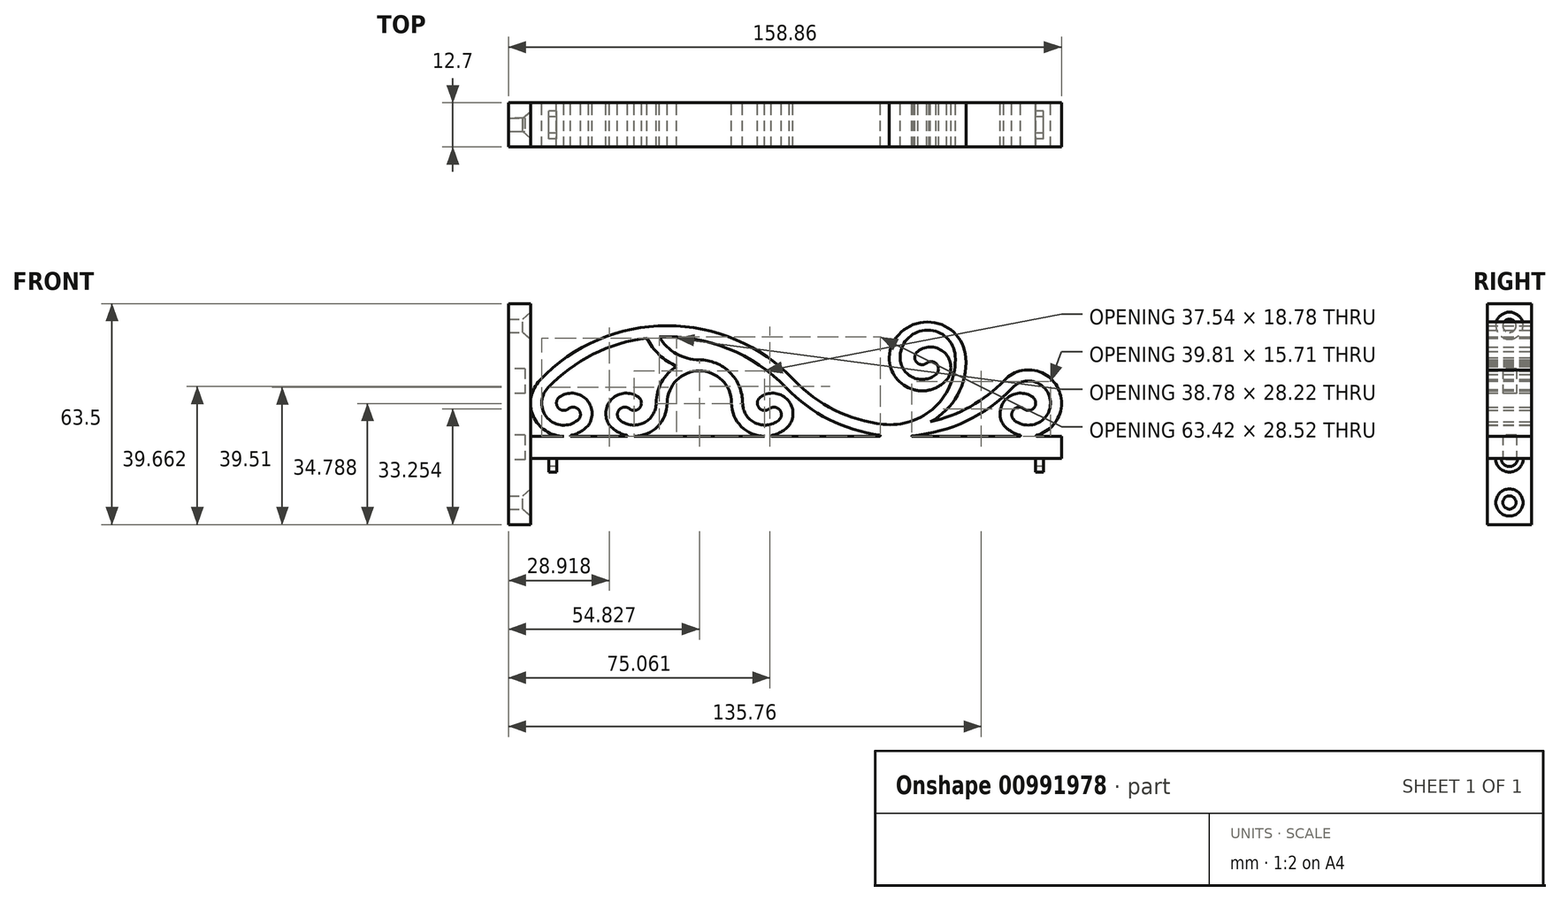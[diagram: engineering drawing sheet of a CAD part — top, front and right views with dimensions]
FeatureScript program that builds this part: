
annotation { "Feature Type Name" : "Feature", "Feature Type Description" : "" }
export const myFeature = defineFeature(function(context is Context, id is Id, definition is map)
    precondition{}
    {
        {
            var Q0;
            Q0=qCreatedBy(makeId("Front.planeOp"),FACE);
            var sketch = newSketch(context, id + "F0", { "sketchPlane" : qUnion([Q0])});
            skLineSegment(sketch, "E0.bottom", {"start": v(-3.17, 31.75) * mm, "end": v(3.18, 31.75) * mm, "construction": true});
            skLineSegment(sketch, "E0.top", {"start": v(-3.17, -31.75) * mm, "end": v(3.18, -31.75) * mm, "construction": true});
            skLineSegment(sketch, "E0.right", {"start": v(3.18, 31.75) * mm, "end": v(3.18, -31.75) * mm});
            skPoint(sketch, "E0.middle", {"position": v(0, 0) * mm});
            skLineSegment(sketch, "E1", {"start": v(3.18, 31.75) * mm, "end": v(-3.17, 31.75) * mm});
            skLineSegment(sketch, "E2", {"start": v(3.18, -31.75) * mm, "end": v(-3.17, -31.75) * mm});
            skLineSegment(sketch, "E3", {"start": v(-3.17, 31.75) * mm, "end": v(-3.17, -31.75) * mm});
            skSolve(sketch);
        }
        {
            var Q0;
            Q0=makeQuery(id+"F0.imprint","IMPRINT",FACE,{"disambiguationData":[TD([[makeQuery(id+"F0.imprint","IMPRINT",EDGE,{"derivedFrom":sQuery(id+"F0.wireOp",EDGE,"E0.right")}),-1.0]])]});
            extrude(context, id + "F1", {"entities" : qUnion([Q0]), "endBound" : BoundingType.SYMMETRIC, "depth" : 12.7 * mm});
        }
        {
            var Q0;
            Q0=makeQuery(id+"F1.opExtrude","SWEPT_FACE",FACE,{"disambiguationData":[OSD([sQuery(id+"F0.wireOp",EDGE,"E3")])]});
            var sketch = newSketch(context, id + "F2", { "sketchPlane" : qUnion([Q0])});
            skLineSegment(sketch, "E4", {"start": v(0, 9.53) * mm, "end": v(0, -9.53) * mm, "construction": true});
            skLineSegment(sketch, "E5.bottom", {"start": v(-1.97, 13.08) * mm, "end": v(1.97, 13.08) * mm});
            skLineSegment(sketch, "E5.top", {"start": v(-1.97, 5.97) * mm, "end": v(1.97, 5.97) * mm});
            skLineSegment(sketch, "E5.left", {"start": v(-1.97, 13.08) * mm, "end": v(-1.97, 5.97) * mm});
            skLineSegment(sketch, "E5.right", {"start": v(1.97, 13.08) * mm, "end": v(1.97, 5.97) * mm});
            skPoint(sketch, "E5.middle", {"position": v(0, 9.53) * mm});
            skLineSegment(sketch, "E6.bottom", {"start": v(-1.97, -5.97) * mm, "end": v(1.97, -5.97) * mm});
            skLineSegment(sketch, "E6.top", {"start": v(-1.97, -13.08) * mm, "end": v(1.97, -13.08) * mm});
            skLineSegment(sketch, "E6.left", {"start": v(-1.97, -5.97) * mm, "end": v(-1.97, -13.08) * mm});
            skLineSegment(sketch, "E6.right", {"start": v(1.97, -5.97) * mm, "end": v(1.97, -13.08) * mm});
            skPoint(sketch, "E6.middle", {"position": v(0, -9.53) * mm});
            skSolve(sketch);
        }
        {
            var Q0;
            Q0=makeQuery(id+"F2.imprint","IMPRINT",FACE,{"disambiguationData":[TD([[makeQuery(id+"F2.imprint","IMPRINT",EDGE,{"derivedFrom":sQuery(id+"F2.wireOp",EDGE,"E5.bottom")}),-1.0]])]});
            var Q1;
            Q1=makeQuery(id+"F2.imprint","IMPRINT",FACE,{"disambiguationData":[TD([[makeQuery(id+"F2.imprint","IMPRINT",EDGE,{"derivedFrom":sQuery(id+"F2.wireOp",EDGE,"E6.bottom")}),-1.0]])]});
            extrude(context, id + "F3", {"entities" : qUnion([Q0, Q1]), "operationType" : NewBodyOperationType.REMOVE, "oppositeDirection" : true, "depth" : 4.76 * mm});
        }
        {
            var Q0;
            Q0=makeQuery(id+"F1.opExtrude","SWEPT_FACE",FACE,{"disambiguationData":[OSD([sQuery(id+"F0.wireOp",EDGE,"E0.right")])]});
            var sketch = newSketch(context, id + "F4", { "sketchPlane" : qUnion([Q0])});
            skLineSegment(sketch, "E7", {"start": v(0, 25.4) * mm, "end": v(0, -25.4) * mm, "construction": true});
            skPoint(sketch, "E8", {"position": v(0, 25.4) * mm});
            skPoint(sketch, "E9", {"position": v(0, -25.4) * mm});
            skSolve(sketch);
        }
        {
            var Q0;
            Q0=sQuery(id+"F4.wireOp",VERTEX,"E8");
            var Q1;
            Q1=sQuery(id+"F4.wireOp",VERTEX,"E9");
            var Q2;
            Q2=makeQuery(id+"F1.opExtrude","SWEPT_BODY",BODY,{"disambiguationData":[OSD([sQuery(id+"F0.wireOp",EDGE,"E0.right"),sQuery(id+"F0.wireOp",EDGE,"E1"),sQuery(id+"F0.wireOp",EDGE,"E2"),sQuery(id+"F0.wireOp",EDGE,"E3")])]});
            hole(context, id + "F5", {"style" : HoleStyle.C_SINK, "endStyle" : HoleEndStyle.THROUGH, "standardTappedOrClearance" : lookupTablePath({ "standard" : "ANSI", "fit" : "Normal (ASME)", "size" : "#6", "type" : "Clearance" }), "standardBlindInLast" : lookupTablePath({ "fit" : "Free", "standard" : "ANSI", "size" : "#6", "type" : "Clearance" }), "holeDiameter" : 3.8 * mm, "cSinkDiameter" : 7.8 * mm, "cSinkAngle" : 82 * degree, "isTappedThrough" : true, "tappedDepth" : 12.7 * mm, "tapClearance" : 3, "locations" : qUnion([Q0, Q1]), "scope" : qUnion([Q2])});
        }
        {
            var Q0;
            Q0=makeQuery(id+"F1.opExtrude","SWEPT_FACE",FACE,{"disambiguationData":[OSD([sQuery(id+"F0.wireOp",EDGE,"E0.right")])]});
            var sketch = newSketch(context, id + "F6", { "sketchPlane" : qUnion([Q0])});
            skLineSegment(sketch, "E10.bottom", {"start": v(-6.35, 12.7) * mm, "end": v(6.35, 12.7) * mm});
            skLineSegment(sketch, "E10.top", {"start": v(-6.35, -12.7) * mm, "end": v(6.35, -12.7) * mm});
            skLineSegment(sketch, "E10.left", {"start": v(-6.35, 12.7) * mm, "end": v(-6.35, -12.7) * mm});
            skLineSegment(sketch, "E10.right", {"start": v(6.35, 12.7) * mm, "end": v(6.35, -12.7) * mm});
            skPoint(sketch, "E10.middle", {"position": v(0, 0) * mm});
            skSolve(sketch);
        }
        {
            var Q0;
            Q0=qCreatedBy(makeId("Front.planeOp"),FACE);
            var sketch = newSketch(context, id + "F7", { "sketchPlane" : qUnion([Q0])});
            skLineSegment(sketch, "E11.bottom", {"start": v(3.18, -6.35) * mm, "end": v(12.7, -6.35) * mm});
            skLineSegment(sketch, "E11.top", {"start": v(3.18, -12.7) * mm, "end": v(14.29, -12.7) * mm});
            skLineSegment(sketch, "E11.left", {"start": v(3.18, -6.35) * mm, "end": v(3.18, -12.7) * mm});
            skLineSegment(sketch, "E11.right", {"start": v(155.68, -6.35) * mm, "end": v(155.68, -12.7) * mm});
            skLineSegment(sketch, "E12", {"start": v(0, 0) * mm, "end": v(3.22, 0) * mm, "construction": true});
            skArc(sketch, "E13", {"start": v(5.8, 9.75) * mm, "mid": v(3.94, -0.57) * mm, "end": v(12.7, -6.35) * mm});
            skArc(sketch, "E14", {"start": v(8.1, 7.56) * mm, "mid": v(8.03, -1.13) * mm, "end": v(16.69, -1.77) * mm});
            skArc(sketch, "E15", {"start": v(11.44, 4.87) * mm, "mid": v(11.03, 1.88) * mm, "end": v(14.03, 1.53) * mm});
            skArc(sketch, "E16", {"start": v(16.69, -1.77) * mm, "mid": v(17, 1.21) * mm, "end": v(14.03, 1.53) * mm});
            skArc(sketch, "E17", {"start": v(19.77, -3.21) * mm, "mid": v(19.04, 4.36) * mm, "end": v(11.44, 4.87) * mm});
            skArc(sketch, "E18", {"start": v(78.9, 9.75) * mm, "mid": v(42.36, 25.4) * mm, "end": v(5.8, 9.75) * mm});
            skArc(sketch, "E19", {"start": v(76.6, 7.56) * mm, "mid": v(59.98, 18.82) * mm, "end": v(40.17, 22.17) * mm});
            skLineSegment(sketch, "E20", {"start": v(42.36, 25.4) * mm, "end": v(79.43, 25.4) * mm, "construction": true});
            skLineSegment(sketch, "E21", {"start": v(79.43, -6.35) * mm, "end": v(79.43, 38.2) * mm, "construction": true});
            skArc(sketch, "E22.MirrorCS", {"start": v(141.55, 7.56) * mm, "mid": v(152.49, 3.59) * mm, "end": v(142.16, -1.77) * mm});
            skArc(sketch, "E23.MirrorC", {"start": v(139.26, 9.75) * mm, "mid": v(154.38, 7.97) * mm, "end": v(148.47, -6.06) * mm});
            skArc(sketch, "E24.MirrorCS", {"start": v(147.4, 4.87) * mm, "mid": v(147.82, 1.88) * mm, "end": v(144.82, 1.53) * mm});
            skArc(sketch, "E25.MirrorCS", {"start": v(142.16, -1.77) * mm, "mid": v(141.84, 1.21) * mm, "end": v(144.82, 1.53) * mm});
            skArc(sketch, "E26.MirrorCS", {"start": v(139.08, -3.21) * mm, "mid": v(139.81, 4.36) * mm, "end": v(147.4, 4.87) * mm});
            skArc(sketch, "E27", {"start": v(78.9, 9.75) * mm, "mid": v(90.56, 1.17) * mm, "end": v(104.44, -2.92) * mm});
            skArc(sketch, "E28", {"start": v(76.6, 7.56) * mm, "mid": v(88.85, -1.53) * mm, "end": v(103.44, -6) * mm});
            skPoint(sketch, "E29.orphan", {"position": v(18.91, 4.48) * mm});
            skPoint(sketch, "E30.orphan", {"position": v(139.94, 4.48) * mm});
            skArc(sketch, "E31", {"start": v(103.41, -6.35) * mm, "mid": v(103.6, -6.18) * mm, "end": v(103.44, -6) * mm});
            skArc(sketch, "E32", {"start": v(112.74, -6.2) * mm, "mid": v(112.67, -6.28) * mm, "end": v(112.75, -6.35) * mm});
            skArc(sketch, "E33.trimOffspring", {"start": v(112.74, -6.2) * mm, "mid": v(128.41, -1.97) * mm, "end": v(141.55, 7.56) * mm});
            skLineSegment(sketch, "E34.trimOffspring", {"start": v(112.75, -6.35) * mm, "end": v(143.75, -6.35) * mm});
            skArc(sketch, "E35", {"start": v(148.47, -6.06) * mm, "mid": v(148.36, -6.22) * mm, "end": v(148.5, -6.35) * mm});
            skArc(sketch, "E36", {"start": v(143.75, -6.35) * mm, "mid": v(143.9, -6.22) * mm, "end": v(143.8, -6.05) * mm});
            skArc(sketch, "E37.trimOffspring", {"start": v(143.8, -6.05) * mm, "mid": v(141.23, -4.98) * mm, "end": v(139.08, -3.21) * mm});
            skLineSegment(sketch, "E38.trimOffspring", {"start": v(148.5, -6.35) * mm, "end": v(155.68, -6.35) * mm});
            skLineSegment(sketch, "E39", {"start": v(12.7, -6.35) * mm, "end": v(12.7, -6.35) * mm});
            skArc(sketch, "E40", {"start": v(14.67, -6.14) * mm, "mid": v(14.58, -6.26) * mm, "end": v(14.69, -6.35) * mm});
            skArc(sketch, "E41.trimOffspring", {"start": v(14.67, -6.14) * mm, "mid": v(17.45, -5.08) * mm, "end": v(19.77, -3.21) * mm});
            skLineSegment(sketch, "E42.trimOffspring", {"start": v(14.69, -6.35) * mm, "end": v(70.42, -6.35) * mm});
            skLineSegment(sketch, "E43", {"start": v(42.36, 25.4) * mm, "end": v(3.22, 25.4) * mm, "construction": true});
            skLineSegment(sketch, "E44", {"start": v(22.79, 25.4) * mm, "end": v(22.79, -6.35) * mm, "construction": true});
            skArc(sketch, "E45.MirrorCS", {"start": v(28.9, -1.77) * mm, "mid": v(28.57, 1.21) * mm, "end": v(31.55, 1.53) * mm});
            skLineSegment(sketch, "E46.MirrorCS", {"start": v(32.88, -6.35) * mm, "end": v(32.88, -6.35) * mm});
            skPoint(sketch, "E47.MirrorP", {"position": v(26.66, 4.48) * mm});
            skArc(sketch, "E48.MirrorCS", {"start": v(30.91, -6.14) * mm, "mid": v(31, -6.26) * mm, "end": v(30.9, -6.35) * mm});
            skLineSegment(sketch, "E49.MirrorCS", {"start": v(42.4, -6.35) * mm, "end": v(32.88, -6.35) * mm});
            skLineSegment(sketch, "E50.MirrorCS", {"start": v(45.58, 0) * mm, "end": v(42.36, 0) * mm, "construction": true});
            skArc(sketch, "E51.MirrorCS", {"start": v(39.23, 3.18) * mm, "mid": v(35.62, -2.55) * mm, "end": v(28.9, -1.77) * mm});
            skArc(sketch, "E52.MirrorCS", {"start": v(30.91, -6.14) * mm, "mid": v(28.13, -5.08) * mm, "end": v(25.81, -3.21) * mm});
            skArc(sketch, "E53.MirrorCS", {"start": v(34.13, 4.87) * mm, "mid": v(34.55, 1.88) * mm, "end": v(31.55, 1.53) * mm});
            skArc(sketch, "E54.MirrorCS", {"start": v(25.81, -3.21) * mm, "mid": v(26.54, 4.36) * mm, "end": v(34.13, 4.87) * mm});
            skLineSegment(sketch, "E55", {"start": v(42.36, 25.4) * mm, "end": v(42.4, -6.35) * mm, "construction": true});
            skLineSegment(sketch, "E56", {"start": v(60.9, 25.4) * mm, "end": v(60.9, -6.35) * mm, "construction": true});
            skLineSegment(sketch, "E57", {"start": v(60.9, 25.4) * mm, "end": v(42.4, -6.35) * mm, "construction": true});
            skLineSegment(sketch, "E58", {"start": v(51.65, 9.53) * mm, "end": v(51.65, 17.18) * mm, "construction": true});
            skArc(sketch, "E59.MirrorCS", {"start": v(64.07, 3.18) * mm, "mid": v(67.68, -2.55) * mm, "end": v(74.4, -1.77) * mm});
            skArc(sketch, "E60.MirrorCS", {"start": v(74.4, -1.77) * mm, "mid": v(74.72, 1.21) * mm, "end": v(71.74, 1.53) * mm});
            skArc(sketch, "E61.MirrorCS", {"start": v(72.38, -6.14) * mm, "mid": v(75.16, -5.08) * mm, "end": v(77.48, -3.21) * mm});
            skLineSegment(sketch, "E62.MirrorCS", {"start": v(70.42, -6.35) * mm, "end": v(70.42, -6.35) * mm});
            skPoint(sketch, "E63.MirrorP", {"position": v(76.63, 4.48) * mm});
            skArc(sketch, "E64.MirrorCS", {"start": v(69.16, 4.87) * mm, "mid": v(68.74, 1.88) * mm, "end": v(71.74, 1.53) * mm});
            skArc(sketch, "E65.MirrorCS", {"start": v(72.38, -6.14) * mm, "mid": v(72.3, -6.26) * mm, "end": v(72.4, -6.35) * mm});
            skArc(sketch, "E66.MirrorCS", {"start": v(77.48, -3.21) * mm, "mid": v(76.75, 4.36) * mm, "end": v(69.16, 4.87) * mm});
            skLineSegment(sketch, "E67.MirrorCS", {"start": v(60.9, -6.35) * mm, "end": v(70.42, -6.35) * mm});
            skArc(sketch, "E68", {"start": v(60.9, 3.18) * mm, "mid": v(51.64, 12.43) * mm, "end": v(42.39, 3.18) * mm});
            skArc(sketch, "E69", {"start": v(64.07, 3.18) * mm, "mid": v(60.42, 11.97) * mm, "end": v(51.62, 15.6) * mm});
            skLineSegment(sketch, "E70", {"start": v(51.65, 9.53) * mm, "end": v(26.5, 9.75) * mm, "construction": true});
            skArc(sketch, "E71", {"start": v(40.17, 22.17) * mm, "mid": v(45.01, 17.35) * mm, "end": v(51.62, 15.6) * mm});
            skArc(sketch, "E72", {"start": v(36.56, 21.87) * mm, "mid": v(40.1, 17.03) * mm, "end": v(45.13, 13.74) * mm});
            skArc(sketch, "E73.trimOffspring", {"start": v(36.56, 21.87) * mm, "mid": v(21.1, 17.18) * mm, "end": v(8.1, 7.56) * mm});
            skArc(sketch, "E74.trimOffspring", {"start": v(45.13, 13.74) * mm, "mid": v(40.8, 9.23) * mm, "end": v(39.23, 3.18) * mm});
            skPoint(sketch, "E75.orphan", {"position": v(51.64, 12.43) * mm});
            skArc(sketch, "E76.trimOffspring", {"start": v(42.39, 3.18) * mm, "mid": v(39.6, -3.56) * mm, "end": v(32.88, -6.35) * mm});
            skPoint(sketch, "E77.orphan", {"position": v(37.47, 7.56) * mm});
            skPoint(sketch, "E78.MirrorCS.start.orphan", {"position": v(39.77, 9.75) * mm});
            skArc(sketch, "E79.trimOffspring", {"start": v(60.9, 3.18) * mm, "mid": v(63.68, -3.56) * mm, "end": v(70.42, -6.35) * mm});
            skPoint(sketch, "E80.MirrorCS.start.orphan", {"position": v(63.52, 9.75) * mm});
            skPoint(sketch, "E81.orphan", {"position": v(65.82, 7.56) * mm});
            skLineSegment(sketch, "E82.trimOffspring", {"start": v(72.4, -6.35) * mm, "end": v(103.41, -6.35) * mm});
            skArc(sketch, "E83.MirrorCS", {"start": v(109.3, 16.67) * mm, "mid": v(112.74, 10.67) * mm, "end": v(119.62, 11.38) * mm});
            skArc(sketch, "E84.MirrorCS", {"start": v(119.62, 11.38) * mm, "mid": v(119.87, 14.3) * mm, "end": v(116.97, 14.67) * mm});
            skArc(sketch, "E85.MirrorCS", {"start": v(117.61, 6.91) * mm, "mid": v(120.4, 7.98) * mm, "end": v(122.71, 9.85) * mm});
            skPoint(sketch, "E86.MirrorP", {"position": v(121.85, 17.33) * mm});
            skArc(sketch, "E87.MirrorCS", {"start": v(114.38, 18.01) * mm, "mid": v(113.97, 15.02) * mm, "end": v(116.97, 14.67) * mm});
            skArc(sketch, "E88.MirrorCS", {"start": v(122.71, 9.85) * mm, "mid": v(122.14, 17.6) * mm, "end": v(114.38, 18.01) * mm});
            skArc(sketch, "E89.trimOffspring", {"start": v(106.12, 16.23) * mm, "mid": v(108.08, 10.44) * mm, "end": v(113.16, 7.04) * mm});
            skArc(sketch, "E90", {"start": v(113.16, 7.04) * mm, "mid": v(115.38, 6.66) * mm, "end": v(117.61, 6.91) * mm});
            skArc(sketch, "E91", {"start": v(128.16, 16.23) * mm, "mid": v(117.14, 26.48) * mm, "end": v(106.12, 16.23) * mm});
            skArc(sketch, "E92", {"start": v(125.13, 16.67) * mm, "mid": v(117.22, 24.15) * mm, "end": v(109.3, 16.67) * mm});
            skArc(sketch, "E93", {"start": v(104.44, -2.92) * mm, "mid": v(119.33, 2.07) * mm, "end": v(125.13, 16.67) * mm});
            skArc(sketch, "E94", {"start": v(117.96, -2.22) * mm, "mid": v(125.8, 5.49) * mm, "end": v(128.16, 16.23) * mm});
            skArc(sketch, "E95.trimOffspring", {"start": v(117.96, -2.22) * mm, "mid": v(129.5, 2.17) * mm, "end": v(139.26, 9.75) * mm});
            skLineSegment(sketch, "E96.trimOffspring", {"start": v(144.56, -12.7) * mm, "end": v(155.68, -12.7) * mm});
            skLineSegment(sketch, "E97.MirrorCS", {"start": v(14.29, -12.7) * mm, "end": v(14.29, -12.7) * mm});
            skLineSegment(sketch, "E98.trimOffspring", {"start": v(14.29, -12.7) * mm, "end": v(144.56, -12.7) * mm});
            skSolve(sketch);
        }
        {
            var Q0;
            Q0=makeQuery(id+"F7.imprint","IMPRINT",FACE,{"disambiguationData":[TD([[makeQuery(id+"F7.imprint","IMPRINT",EDGE,{"derivedFrom":sQuery(id+"F7.wireOp",EDGE,"E11.bottom")}),-1.0]])]});
            extrude(context, id + "F8", {"entities" : qUnion([Q0]), "endBound" : BoundingType.SYMMETRIC, "depth" : 12.7 * mm});
        }
        {
            var Q0;
            Q0=makeQuery(id+"F8.opExtrude","SWEPT_FACE",FACE,{"disambiguationData":[OSD([sQuery(id+"F7.wireOp",EDGE,"E11.right")])]});
            cPlane(context, id + "F9", {"entities" : qUnion([Q0]), "cplaneType" : CPlaneType.OFFSET, "offset" : 6.35 * mm, "oppositeDirection" : true, "width" : 152.4 * mm, "height" : 152.4 * mm});
        }
        {
            var Q0;
            Q0=qCreatedBy(id+"F9.planeOp",FACE);
            var sketch = newSketch(context, id + "F10", { "sketchPlane" : qUnion([Q0])});
            skArc(sketch, "E99", {"start": v(-3.97, -12.7) * mm, "mid": v(0, -16.67) * mm, "end": v(3.97, -12.7) * mm});
            skLineSegment(sketch, "E100", {"start": v(-3.97, -12.7) * mm, "end": v(-3.97, -10.42) * mm, "construction": true});
            skLineSegment(sketch, "E101", {"start": v(-3.97, -10.42) * mm, "end": v(3.97, -10.42) * mm, "construction": true});
            skLineSegment(sketch, "E102", {"start": v(3.97, -10.42) * mm, "end": v(3.97, -12.7) * mm, "construction": true});
            skArc(sketch, "E103.0", {"start": v(-2.38, -12.7) * mm, "mid": v(0, -15.08) * mm, "end": v(2.38, -12.7) * mm});
            skLineSegment(sketch, "E104", {"start": v(-3.97, -12.7) * mm, "end": v(-2.38, -12.7) * mm});
            skLineSegment(sketch, "E105", {"start": v(2.38, -12.7) * mm, "end": v(3.97, -12.7) * mm});
            skSolve(sketch);
        }
        {
            var Q0;
            Q0=makeQuery(id+"F10.imprint","IMPRINT",FACE,{"disambiguationData":[TD([[makeQuery(id+"F10.imprint","IMPRINT",EDGE,{"derivedFrom":sQuery(id+"F10.wireOp",EDGE,"E99")}),1.0]])]});
            extrude(context, id + "F11", {"entities" : qUnion([Q0]), "operationType" : NewBodyOperationType.ADD, "endBound" : BoundingType.SYMMETRIC, "depth" : 2.3 * mm});
        }
        {
            var Q0;
            {var subQ3=sQuery(id+"F6.wireOp",EDGE,"E10.top");Q0=makeQuery(id+"F6.imprint","IMPRINT",FACE,{"disambiguationData":[TD([[makeQuery(id+"F6.imprint","IMPRINT",EDGE,{"derivedFrom":subQ3}),-1.0]])]});}
            cPlane(context, id + "F12", {"entities" : qUnion([Q0]), "cplaneType" : CPlaneType.OFFSET, "offset" : 6.35 * mm, "width" : 152.4 * mm, "height" : 152.4 * mm});
        }
        {
            var Q0;
            Q0=qCreatedBy(id+"F12.planeOp",FACE);
            var sketch = newSketch(context, id + "F13", { "sketchPlane" : qUnion([Q0])});
            skArc(sketch, "E106.0", {"start": v(-2.38, -12.7) * mm, "mid": v(0, -15.08) * mm, "end": v(2.38, -12.7) * mm});
            skLineSegment(sketch, "E106.1", {"start": v(-3.97, -12.7) * mm, "end": v(-2.38, -12.7) * mm});
            skLineSegment(sketch, "E106.2", {"start": v(2.38, -12.7) * mm, "end": v(3.97, -12.7) * mm});
            skArc(sketch, "E106.3", {"start": v(-3.97, -12.7) * mm, "mid": v(0, -16.67) * mm, "end": v(3.97, -12.7) * mm});
            skSolve(sketch);
        }
        {
            var Q0;
            Q0=qSketchRegion(id+"F13",true);
            extrude(context, id + "F14", {"entities" : qUnion([Q0]), "operationType" : NewBodyOperationType.ADD, "endBound" : BoundingType.SYMMETRIC, "depth" : 2.3 * mm});
        }
    });
